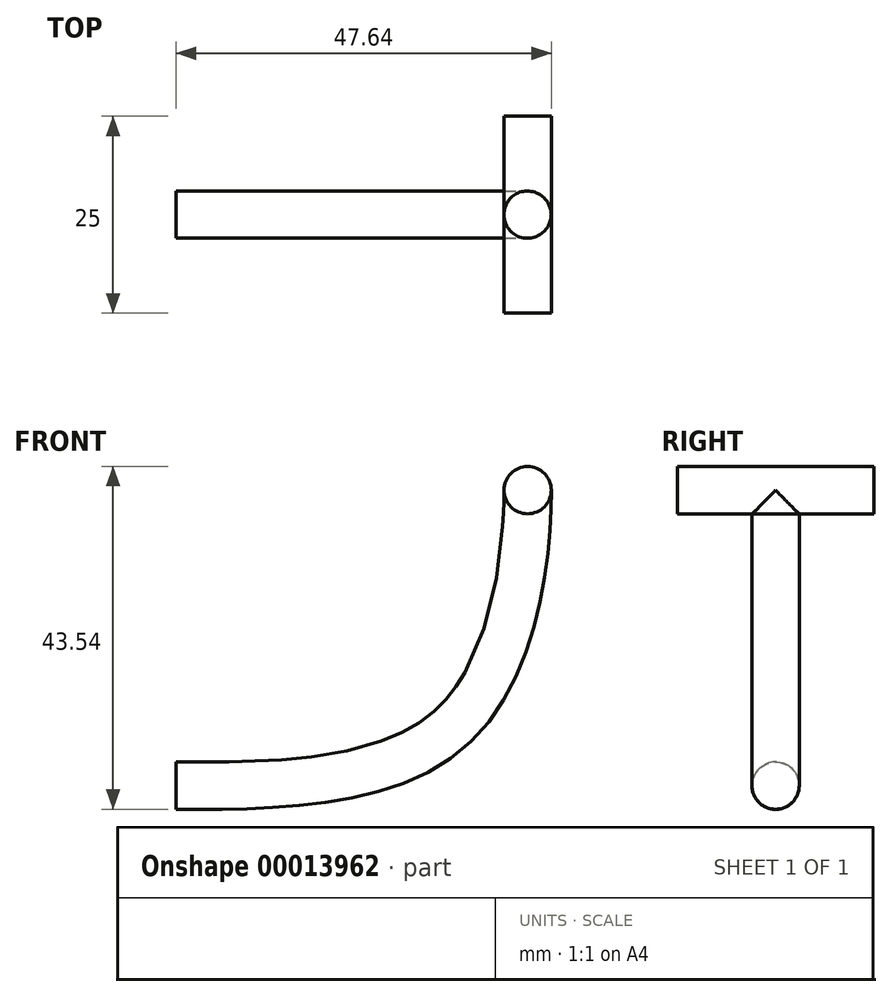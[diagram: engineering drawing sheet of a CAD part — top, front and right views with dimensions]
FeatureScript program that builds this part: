
annotation { "Feature Type Name" : "Feature", "Feature Type Description" : "" }
export const myFeature = defineFeature(function(context is Context, id is Id, definition is map)
    precondition{}
    {
        {
            var Q0;
            Q0=qCreatedBy(makeId("Front.planeOp"),FACE);
            var sketch = newSketch(context, id + "F0", { "sketchPlane" : qUnion([Q0])});
            skFitSpline(sketch, "E0", {"points": [v(-44.64, 0) * mm, v(-9.52, 7.5) * mm, v(0, 37.54) * mm], "startDerivative": vector(62.13, 0) * mm, "endDerivative": vector(0, 50.09) * mm});
            skSolve(sketch);
        }
        {
            var Q0;
            Q0=sQuery(id+"F0.wireOp",VERTEX,"E0.start");
            var Q1;
            Q1=qCreatedBy(makeId("Right.planeOp"),FACE);
            cPlane(context, id + "F1", {"entities" : qUnion([Q0, Q1]), "cplaneType" : CPlaneType.PLANE_POINT, "offset" : 150 * mm, "width" : 150 * mm, "height" : 150 * mm});
        }
        {
            var Q0;
            Q0=qCreatedBy(makeId("Front.planeOp"),FACE);
            var sketch = newSketch(context, id + "F2", { "sketchPlane" : qUnion([Q0])});
            skCircle(sketch, "E1", {"center": v(0, 37.54) * mm, "radius": 3 * mm});
            skSolve(sketch);
        }
        {
            var Q0;
            Q0=makeQuery(id+"F2.imprint","IMPRINT",FACE,{"disambiguationData":[TD([[makeQuery(id+"F2.imprint","IMPRINT",EDGE,{"derivedFrom":sQuery(id+"F2.wireOp",EDGE,"E1")}),1.0]])]});
            var Q1;
            Q1=sQuery(id+"F2.wireOp",EDGE,"E1");
            extrude(context, id + "F3", {"entities" : qUnion([Q0]), "surfaceEntities" : qUnion([Q1]), "depth" : 25 * mm, "symmetric" : true});
        }
        {
            var Q0;
            Q0=qCreatedBy(id+"F1.planeOp",FACE);
            var sketch = newSketch(context, id + "F4", { "sketchPlane" : qUnion([Q0])});
            skCircle(sketch, "E2", {"center": v(0, 0) * mm, "radius": 3 * mm});
            skSolve(sketch);
        }
        {
            var Q0;
            Q0=makeQuery(id+"F4.imprint","IMPRINT",FACE,{"disambiguationData":[TD([[makeQuery(id+"F4.imprint","IMPRINT",EDGE,{"derivedFrom":sQuery(id+"F4.wireOp",EDGE,"E2")}),1.0]])]});
            var Q1;
            Q1=sQuery(id+"F0.wireOp",EDGE,"E0");
            sweep(context, id + "F5", {"profiles" : qUnion([Q0]), "path" : qUnion([Q1])});
        }
        {
            var Q0;
            Q0=makeQuery(id+"F3.opExtrude","SWEPT_BODY",BODY,{"disambiguationData":[OSD([sQuery(id+"F2.wireOp",EDGE,"E1")])]});
            var Q1;
            Q1=makeQuery(id+"F5.opSweep","SWEPT_BODY",BODY,{"disambiguationData":[OSD([sQuery(id+"F0.wireOp",EDGE,"E0"),sQuery(id+"F4.wireOp",EDGE,"E2")])]});
            booleanBodies(context, id + "F6", {"operationType" : BooleanOperationType.SUBTRACTION, "tools" : qUnion([Q0]), "targets" : qUnion([Q1]), "keepTools" : true});
        }
    });
